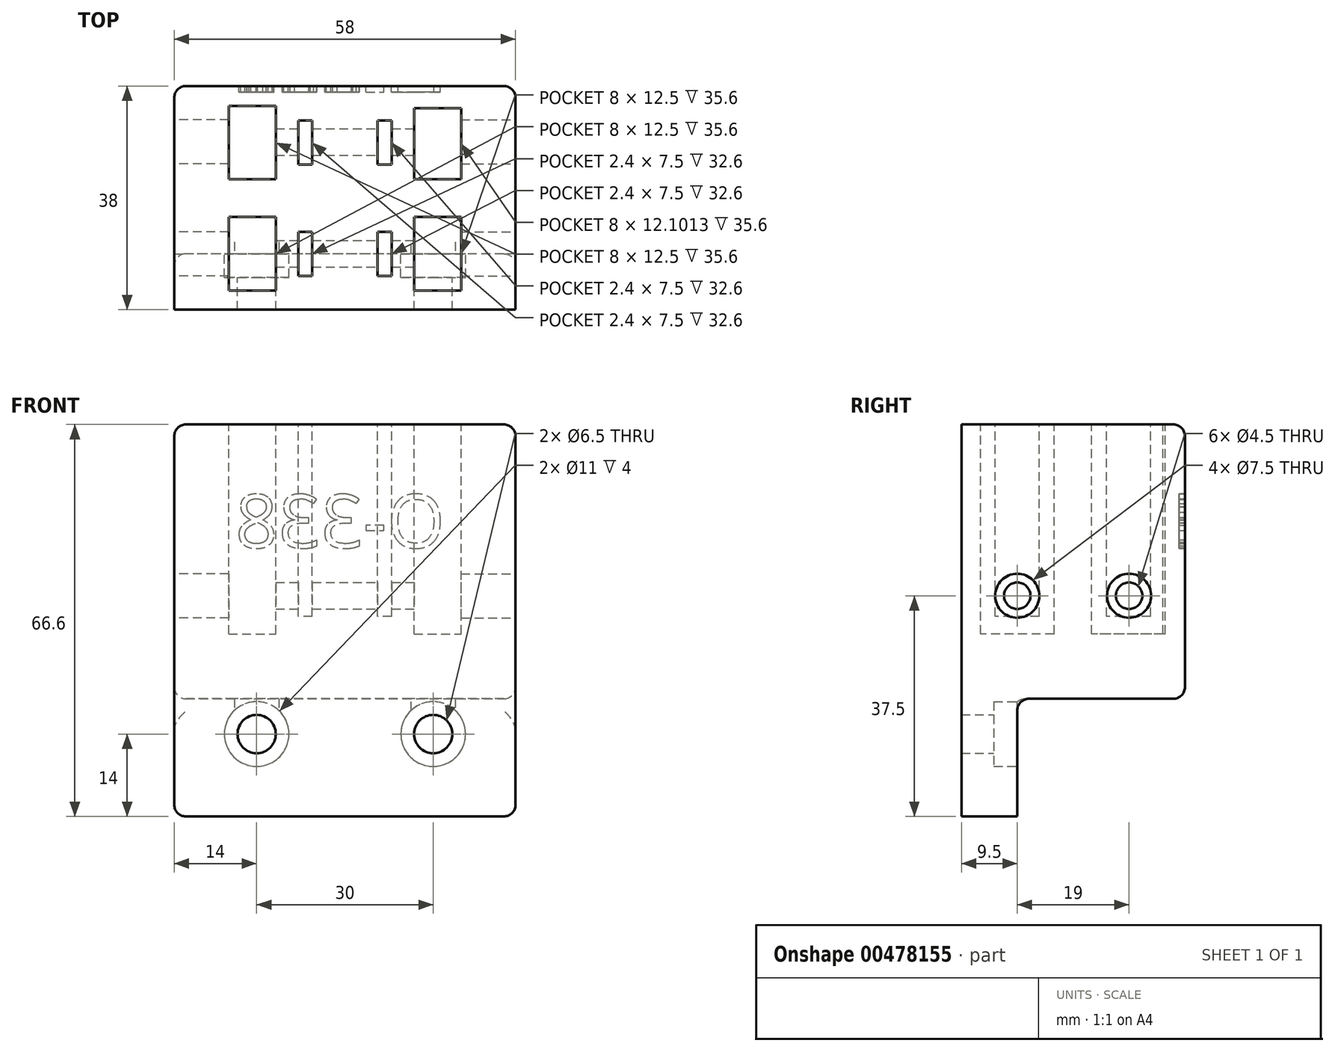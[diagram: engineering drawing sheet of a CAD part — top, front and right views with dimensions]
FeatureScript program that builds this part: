
annotation { "Feature Type Name" : "Feature", "Feature Type Description" : "" }
export const myFeature = defineFeature(function(context is Context, id is Id, definition is map)
    precondition{}
    {
        {
            var Q0;
            Q0=qCreatedBy(makeId("Top.planeOp"),FACE);
            var sketch = newSketch(context, id + "F0", { "sketchPlane" : qUnion([Q0])});
            skLineSegment(sketch, "E0.bottom", {"start": v(-29, 9.5) * mm, "end": v(29, 9.5) * mm});
            skLineSegment(sketch, "E0.top", {"start": v(-29, -9.5) * mm, "end": v(29, -9.5) * mm});
            skLineSegment(sketch, "E0.left", {"start": v(-29, 9.5) * mm, "end": v(-29, -9.5) * mm});
            skLineSegment(sketch, "E0.right", {"start": v(29, 9.5) * mm, "end": v(29, -9.5) * mm});
            skSolve(sketch);
        }
        {
            var Q0;
            Q0 = qSketchRegion(id + "F0", true);
            extrude(context, id + "F1", {"entities" : qUnion([Q0]), "depth" : 11 * mm});
        }
        {
            var Q0;
            Q0=makeQuery(id+"F1.opExtrude","CAP_FACE",FACE,{"disambiguationData":[OSD([sQuery(id+"F0.wireOp",EDGE,"E0.bottom"),sQuery(id+"F0.wireOp",EDGE,"E0.top"),sQuery(id+"F0.wireOp",EDGE,"E0.left"),sQuery(id+"F0.wireOp",EDGE,"E0.right"),sQuery(id+"F0.wireOp",EDGE,"AuSHMrTt-jpj0-5Ru2-xaIe-a4Oixfi13iDE"),sQuery(id+"F0.wireOp",EDGE,"9J5HWsQ0-lQpk-E1t6-wWkI-SOKKZm0BYfsw"),sQuery(id+"F0.wireOp",EDGE,"2GzKSPJo-uI2N-Esed-kJXd-WJqO7sIm6bVz"),sQuery(id+"F0.wireOp",EDGE,"DJKESrdY-mQTo-sUHj-6MfV-pHmhVGQO2tIG")])],"isStart":false});
            var sketch = newSketch(context, id + "F2", { "sketchPlane" : qUnion([Q0])});
            skLineSegment(sketch, "E1.bottom", {"start": v(-29, 9.5) * mm, "end": v(29, 9.5) * mm});
            skLineSegment(sketch, "E1.top", {"start": v(-29, -9.5) * mm, "end": v(29, -9.5) * mm});
            skLineSegment(sketch, "E1.left", {"start": v(-29, 9.5) * mm, "end": v(-29, -9.5) * mm});
            skLineSegment(sketch, "E1.right", {"start": v(29, 9.5) * mm, "end": v(29, -9.5) * mm});
            skPoint(sketch, "E1.middle", {"position": v(0, 0) * mm});
            skSolve(sketch);
        }
        {
            var Q0;
            Q0 = qSketchRegion(id + "F2", true);
            extrude(context, id + "F3", {"entities" : qUnion([Q0]), "operationType" : NewBodyOperationType.ADD, "depth" : 35.6 * mm});
        }
        {
            var Q0;
            Q0=makeQuery(id+"F3.opExtrude","CAP_FACE",FACE,{"disambiguationData":[OSD([sQuery(id+"F2.wireOp",EDGE,"E1.bottom"),sQuery(id+"F2.wireOp",EDGE,"E1.top"),sQuery(id+"F2.wireOp",EDGE,"E1.left"),sQuery(id+"F2.wireOp",EDGE,"E1.right")])],"isStart":false});
            var sketch = newSketch(context, id + "F4", { "sketchPlane" : qUnion([Q0])});
            skLineSegment(sketch, "E2.bottom", {"start": v(-19.75, 6.25) * mm, "end": v(-11.75, 6.25) * mm});
            skLineSegment(sketch, "E2.top", {"start": v(-19.75, -6.25) * mm, "end": v(-11.75, -6.25) * mm});
            skLineSegment(sketch, "E2.left", {"start": v(-19.75, 6.25) * mm, "end": v(-19.75, -6.25) * mm});
            skLineSegment(sketch, "E2.right", {"start": v(-11.75, 6.25) * mm, "end": v(-11.75, -6.25) * mm});
            skPoint(sketch, "E2.middle", {"position": v(-15.75, 0) * mm});
            skLineSegment(sketch, "E3.bottom", {"start": v(11.75, 6.25) * mm, "end": v(19.75, 6.25) * mm});
            skLineSegment(sketch, "E3.top", {"start": v(11.75, -6.25) * mm, "end": v(19.75, -6.25) * mm});
            skLineSegment(sketch, "E3.left", {"start": v(11.75, 6.25) * mm, "end": v(11.75, -6.25) * mm});
            skLineSegment(sketch, "E3.right", {"start": v(19.75, 6.25) * mm, "end": v(19.75, -6.25) * mm});
            skPoint(sketch, "E3.middle", {"position": v(15.75, 0) * mm});
            skSolve(sketch);
        }
        {
            var Q0;
            Q0 = qSketchRegion(id + "F4", true);
            extrude(context, id + "F5", {"entities" : qUnion([Q0]), "operationType" : NewBodyOperationType.REMOVE, "oppositeDirection" : true, "depth" : 35.6 * mm});
        }
        {
            var Q0;
            Q0=makeQuery(id+"F3.boolean.opBoolean","MERGE",FACE,{"derivedFrom":[makeQuery(id+"F1.opExtrude","SWEPT_FACE",FACE,{"disambiguationData":[OSD([sQuery(id+"F0.wireOp",EDGE,"E0.right")])]}),makeQuery(id+"F3.opExtrude","SWEPT_FACE",FACE,{"disambiguationData":[OSD([sQuery(id+"F2.wireOp",EDGE,"E1.right")])]})]});
            var sketch = newSketch(context, id + "F6", { "sketchPlane" : qUnion([Q0])});
            skCircle(sketch, "E4", {"center": v(0, 17.5) * mm, "radius": 2.25 * mm});
            skSolve(sketch);
        }
        {
            var Q0;
            Q0 = qSketchRegion(id + "F6", true);
            extrude(context, id + "F7", {"entities" : qUnion([Q0]), "operationType" : NewBodyOperationType.REMOVE, "endBound" : BoundingType.THROUGH_ALL, "oppositeDirection" : true, "depth" : 25 * mm});
        }
        {
            var Q0;
            Q0=makeQuery(id+"F3.opExtrude","CAP_FACE",FACE,{"disambiguationData":[OSD([sQuery(id+"F2.wireOp",EDGE,"E1.bottom"),sQuery(id+"F2.wireOp",EDGE,"E1.top"),sQuery(id+"F2.wireOp",EDGE,"E1.left"),sQuery(id+"F2.wireOp",EDGE,"E1.right")])],"isStart":false});
            var sketch = newSketch(context, id + "F8", { "sketchPlane" : qUnion([Q0])});
            skLineSegment(sketch, "E5.bottom", {"start": v(7.95, 3.75) * mm, "end": v(5.55, 3.75) * mm});
            skLineSegment(sketch, "E5.top", {"start": v(7.95, -3.75) * mm, "end": v(5.55, -3.75) * mm});
            skLineSegment(sketch, "E5.left", {"start": v(7.95, 3.75) * mm, "end": v(7.95, -3.75) * mm});
            skLineSegment(sketch, "E5.right", {"start": v(5.55, 3.75) * mm, "end": v(5.55, -3.75) * mm});
            skPoint(sketch, "E5.middle", {"position": v(6.75, 0) * mm});
            skLineSegment(sketch, "E6.bottom", {"start": v(-5.55, 3.75) * mm, "end": v(-7.95, 3.75) * mm});
            skLineSegment(sketch, "E6.top", {"start": v(-5.55, -3.75) * mm, "end": v(-7.95, -3.75) * mm});
            skLineSegment(sketch, "E6.left", {"start": v(-5.55, 3.75) * mm, "end": v(-5.55, -3.75) * mm});
            skLineSegment(sketch, "E6.right", {"start": v(-7.95, 3.75) * mm, "end": v(-7.95, -3.75) * mm});
            skPoint(sketch, "E6.middle", {"position": v(-6.75, 0) * mm});
            skSolve(sketch);
        }
        {
            var Q0;
            Q0 = qSketchRegion(id + "F8", true);
            extrude(context, id + "F9", {"entities" : qUnion([Q0]), "operationType" : NewBodyOperationType.REMOVE, "oppositeDirection" : true, "depth" : 32.6 * mm});
        }
        {
            var Q0;
            Q0=makeQuery(id+"F3.boolean.opBoolean","MERGE",FACE,{"derivedFrom":[makeQuery(id+"F1.opExtrude","SWEPT_FACE",FACE,{"disambiguationData":[OSD([sQuery(id+"F0.wireOp",EDGE,"E0.left")])]}),makeQuery(id+"F3.opExtrude","SWEPT_FACE",FACE,{"disambiguationData":[OSD([sQuery(id+"F2.wireOp",EDGE,"E1.left")])]})]});
            var sketch = newSketch(context, id + "F10", { "sketchPlane" : qUnion([Q0])});
            skCircle(sketch, "E7", {"center": v(0, 17.5) * mm, "radius": 3.75 * mm});
            skSolve(sketch);
        }
        {
            var Q0;
            Q0 = qSketchRegion(id + "F10", true);
            extrude(context, id + "F11", {"entities" : qUnion([Q0]), "operationType" : NewBodyOperationType.REMOVE, "oppositeDirection" : true, "depth" : 9.25 * mm});
        }
        {
            var Q0;
            Q0=makeQuery(id+"F3.boolean.opBoolean","MERGE",FACE,{"derivedFrom":[makeQuery(id+"F1.opExtrude","SWEPT_FACE",FACE,{"disambiguationData":[OSD([sQuery(id+"F0.wireOp",EDGE,"E0.right")])]}),makeQuery(id+"F3.opExtrude","SWEPT_FACE",FACE,{"disambiguationData":[OSD([sQuery(id+"F2.wireOp",EDGE,"E1.right")])]})]});
            var sketch = newSketch(context, id + "F12", { "sketchPlane" : qUnion([Q0])});
            skCircle(sketch, "E8", {"center": v(0, 17.5) * mm, "radius": 3.75 * mm});
            skSolve(sketch);
        }
        {
            var Q0;
            Q0 = qSketchRegion(id + "F12", true);
            extrude(context, id + "F13", {"entities" : qUnion([Q0]), "operationType" : NewBodyOperationType.REMOVE, "oppositeDirection" : true, "depth" : 9.25 * mm});
        }
        {
            var Q0;
            Q0 = qSketchRegion(id + "F0", true);
            extrude(context, id + "F14", {"entities" : qUnion([Q0]), "operationType" : NewBodyOperationType.ADD, "oppositeDirection" : true, "depth" : 20 * mm});
        }
        {
            var Q0;
            Q0=qCreatedBy(makeId("Top.planeOp"),FACE);
            var sketch = newSketch(context, id + "F15", { "sketchPlane" : qUnion([Q0])});
            skLineSegment(sketch, "E9.bottom", {"start": v(-29, 28.5) * mm, "end": v(29, 28.5) * mm});
            skLineSegment(sketch, "E9.top", {"start": v(-29, 9.5) * mm, "end": v(29, 9.5) * mm});
            skLineSegment(sketch, "E9.left", {"start": v(-29, 28.5) * mm, "end": v(-29, 9.5) * mm});
            skLineSegment(sketch, "E9.right", {"start": v(29, 28.5) * mm, "end": v(29, 9.5) * mm});
            skSolve(sketch);
        }
        {
            var Q0;
            Q0 = qSketchRegion(id + "F15", true);
            extrude(context, id + "F16", {"entities" : qUnion([Q0]), "operationType" : NewBodyOperationType.ADD, "depth" : 46.6 * mm});
        }
        {
            var Q0;
            Q0=makeQuery(id+"F16.boolean.opBoolean","MERGE",FACE,{"derivedFrom":[makeQuery(id+"F3.opExtrude","CAP_FACE",FACE,{"disambiguationData":[OSD([sQuery(id+"F2.wireOp",EDGE,"E1.bottom"),sQuery(id+"F2.wireOp",EDGE,"E1.top"),sQuery(id+"F2.wireOp",EDGE,"E1.left"),sQuery(id+"F2.wireOp",EDGE,"E1.right")])],"isStart":false}),makeQuery(id+"F16.opExtrude","CAP_FACE",FACE,{"disambiguationData":[OSD([sQuery(id+"F15.wireOp",EDGE,"E9.bottom"),sQuery(id+"F15.wireOp",EDGE,"E9.top"),sQuery(id+"F15.wireOp",EDGE,"E9.left"),sQuery(id+"F15.wireOp",EDGE,"E9.right")])],"isStart":false})]});
            var sketch = newSketch(context, id + "F17", { "sketchPlane" : qUnion([Q0])});
            skLineSegment(sketch, "E10.bottom", {"start": v(-19.75, 25.15) * mm, "end": v(-11.75, 25.15) * mm});
            skLineSegment(sketch, "E10.top", {"start": v(-19.75, 12.65) * mm, "end": v(-11.75, 12.65) * mm});
            skLineSegment(sketch, "E10.left", {"start": v(-19.75, 25.15) * mm, "end": v(-19.75, 12.65) * mm});
            skLineSegment(sketch, "E10.right", {"start": v(-11.75, 25.15) * mm, "end": v(-11.75, 12.65) * mm});
            skLineSegment(sketch, "E11.bottom", {"start": v(11.75, 24.75) * mm, "end": v(19.75, 24.75) * mm});
            skLineSegment(sketch, "E11.top", {"start": v(11.75, 12.65) * mm, "end": v(19.75, 12.65) * mm});
            skLineSegment(sketch, "E11.left", {"start": v(11.75, 24.75) * mm, "end": v(11.75, 12.65) * mm});
            skLineSegment(sketch, "E11.right", {"start": v(19.75, 24.75) * mm, "end": v(19.75, 12.65) * mm});
            skSolve(sketch);
        }
        {
            var Q0;
            Q0 = qSketchRegion(id + "F17", true);
            extrude(context, id + "F18", {"entities" : qUnion([Q0]), "operationType" : NewBodyOperationType.REMOVE, "oppositeDirection" : true, "depth" : 35.6 * mm});
        }
        {
            var Q0;
            {var subQ0=sQuery(id+"F0.wireOp",EDGE,"E0.right");var subQ2=sQuery(id+"F0.wireOp",EDGE,"E0.bottom");var subQ4=sQuery(id+"F2.wireOp",EDGE,"E1.right");Q0=makeQuery(id+"F16.boolean.opBoolean","MERGE",FACE,{"derivedFrom":[makeQuery(id+"F14.boolean.opBoolean","MERGE",FACE,{"derivedFrom":[makeQuery(id+"FXwZepqlZW6l2EH_1.boolean.opBoolean","SPLIT",FACE,{"disambiguationData":[TD([makeQuery(id+"F1.opExtrude","SWEPT_FACE",FACE,{"disambiguationData":[OSD([subQ2])]})])],"derivedFrom":makeQuery(id+"F3.boolean.opBoolean","MERGE",FACE,{"derivedFrom":[makeQuery(id+"F1.opExtrude","SWEPT_FACE",FACE,{"disambiguationData":[OSD([subQ0])]}),makeQuery(id+"F3.opExtrude","SWEPT_FACE",FACE,{"disambiguationData":[OSD([subQ4])]})]})}),makeQuery(id+"F14.opExtrude","SWEPT_FACE",FACE,{"disambiguationData":[OSD([subQ0])]})]}),makeQuery(id+"F16.opExtrude","SWEPT_FACE",FACE,{"disambiguationData":[OSD([sQuery(id+"F15.wireOp",EDGE,"E9.right")])]})]});}
            var sketch = newSketch(context, id + "F19", { "sketchPlane" : qUnion([Q0])});
            skCircle(sketch, "E12", {"center": v(19, 17.5) * mm, "radius": 2.25 * mm});
            skSolve(sketch);
        }
        {
            var Q0;
            Q0 = qSketchRegion(id + "F19", true);
            extrude(context, id + "F20", {"entities" : qUnion([Q0]), "operationType" : NewBodyOperationType.REMOVE, "endBound" : BoundingType.THROUGH_ALL, "oppositeDirection" : true, "depth" : 25 * mm});
        }
        {
            var Q0;
            Q0=makeQuery(id+"F16.boolean.opBoolean","MERGE",FACE,{"derivedFrom":[makeQuery(id+"F3.opExtrude","CAP_FACE",FACE,{"disambiguationData":[OSD([sQuery(id+"F2.wireOp",EDGE,"E1.bottom"),sQuery(id+"F2.wireOp",EDGE,"E1.top"),sQuery(id+"F2.wireOp",EDGE,"E1.left"),sQuery(id+"F2.wireOp",EDGE,"E1.right")])],"isStart":false}),makeQuery(id+"F16.opExtrude","CAP_FACE",FACE,{"disambiguationData":[OSD([sQuery(id+"F15.wireOp",EDGE,"E9.bottom"),sQuery(id+"F15.wireOp",EDGE,"E9.top"),sQuery(id+"F15.wireOp",EDGE,"E9.left"),sQuery(id+"F15.wireOp",EDGE,"E9.right")])],"isStart":false})]});
            var sketch = newSketch(context, id + "F21", { "sketchPlane" : qUnion([Q0])});
            skLineSegment(sketch, "E13.bottom", {"start": v(-7.95, 22.65) * mm, "end": v(-5.55, 22.65) * mm});
            skLineSegment(sketch, "E13.top", {"start": v(-7.95, 15.15) * mm, "end": v(-5.55, 15.15) * mm});
            skLineSegment(sketch, "E13.left", {"start": v(-7.95, 22.65) * mm, "end": v(-7.95, 15.15) * mm});
            skLineSegment(sketch, "E13.right", {"start": v(-5.55, 22.65) * mm, "end": v(-5.55, 15.15) * mm});
            skLineSegment(sketch, "E14.bottom", {"start": v(5.55, 22.65) * mm, "end": v(7.95, 22.65) * mm});
            skLineSegment(sketch, "E14.top", {"start": v(5.55, 15.15) * mm, "end": v(7.95, 15.15) * mm});
            skLineSegment(sketch, "E14.left", {"start": v(5.55, 22.65) * mm, "end": v(5.55, 15.15) * mm});
            skLineSegment(sketch, "E14.right", {"start": v(7.95, 22.65) * mm, "end": v(7.95, 15.15) * mm});
            skSolve(sketch);
        }
        {
            var Q0;
            Q0 = qSketchRegion(id + "F21", true);
            extrude(context, id + "F22", {"entities" : qUnion([Q0]), "operationType" : NewBodyOperationType.REMOVE, "oppositeDirection" : true, "depth" : 32.6 * mm});
        }
        {
            var Q0;
            {var subQ0=sQuery(id+"F0.wireOp",EDGE,"E0.right");var subQ2=sQuery(id+"F0.wireOp",EDGE,"E0.bottom");var subQ4=sQuery(id+"F2.wireOp",EDGE,"E1.right");Q0=makeQuery(id+"F16.boolean.opBoolean","MERGE",FACE,{"derivedFrom":[makeQuery(id+"F14.boolean.opBoolean","MERGE",FACE,{"derivedFrom":[makeQuery(id+"FXwZepqlZW6l2EH_1.boolean.opBoolean","SPLIT",FACE,{"disambiguationData":[TD([makeQuery(id+"F1.opExtrude","SWEPT_FACE",FACE,{"disambiguationData":[OSD([subQ2])]})])],"derivedFrom":makeQuery(id+"F3.boolean.opBoolean","MERGE",FACE,{"derivedFrom":[makeQuery(id+"F1.opExtrude","SWEPT_FACE",FACE,{"disambiguationData":[OSD([subQ0])]}),makeQuery(id+"F3.opExtrude","SWEPT_FACE",FACE,{"disambiguationData":[OSD([subQ4])]})]})}),makeQuery(id+"F14.opExtrude","SWEPT_FACE",FACE,{"disambiguationData":[OSD([subQ0])]})]}),makeQuery(id+"F16.opExtrude","SWEPT_FACE",FACE,{"disambiguationData":[OSD([sQuery(id+"F15.wireOp",EDGE,"E9.right")])]})]});}
            var sketch = newSketch(context, id + "F23", { "sketchPlane" : qUnion([Q0])});
            skCircle(sketch, "E15", {"center": v(19, 17.5) * mm, "radius": 3.75 * mm});
            skSolve(sketch);
        }
        {
            var Q0;
            Q0 = qSketchRegion(id + "F23", true);
            extrude(context, id + "F24", {"entities" : qUnion([Q0]), "operationType" : NewBodyOperationType.REMOVE, "oppositeDirection" : true, "depth" : 10 * mm});
        }
        {
            var Q0;
            {var subQ0=sQuery(id+"F0.wireOp",EDGE,"E0.left");Q0=makeQuery(id+"F16.boolean.opBoolean","MERGE",FACE,{"derivedFrom":[makeQuery(id+"F14.boolean.opBoolean","MERGE",FACE,{"derivedFrom":[makeQuery(id+"F3.boolean.opBoolean","MERGE",FACE,{"derivedFrom":[makeQuery(id+"F1.opExtrude","SWEPT_FACE",FACE,{"disambiguationData":[OSD([subQ0])]}),makeQuery(id+"F3.opExtrude","SWEPT_FACE",FACE,{"disambiguationData":[OSD([sQuery(id+"F2.wireOp",EDGE,"E1.left")])]})]}),makeQuery(id+"F14.opExtrude","SWEPT_FACE",FACE,{"disambiguationData":[OSD([subQ0])]})]}),makeQuery(id+"F16.opExtrude","SWEPT_FACE",FACE,{"disambiguationData":[OSD([sQuery(id+"F15.wireOp",EDGE,"E9.left")])]})]});}
            var sketch = newSketch(context, id + "F25", { "sketchPlane" : qUnion([Q0])});
            skCircle(sketch, "E16", {"center": v(-19, 17.5) * mm, "radius": 3.75 * mm});
            skSolve(sketch);
        }
        {
            var Q0;
            Q0 = qSketchRegion(id + "F25", true);
            extrude(context, id + "F26", {"entities" : qUnion([Q0]), "operationType" : NewBodyOperationType.REMOVE, "oppositeDirection" : true, "depth" : 10 * mm});
        }
        {
            var Q0;
            Q0=makeQuery(id+"F16.opExtrude","SWEPT_FACE",FACE,{"disambiguationData":[OSD([sQuery(id+"F15.wireOp",EDGE,"E9.bottom")])]});
            var sketch = newSketch(context, id + "F27", { "sketchPlane" : qUnion([Q0])});
            skText(sketch, "E17", { "text": "O-338", "fontName": "OpenSans-Regular.ttf"});
            const initialGuessF27  = {"E17": [-0.017, 0.02564, 1, 0, 0.00912]};
            skSetInitialGuess(sketch, initialGuessF27);
            skSolve(sketch);
        }
        {
            var Q0;
            Q0 = qSketchRegion(id + "F27", true);
            extrude(context, id + "F28", {"entities" : qUnion([Q0]), "operationType" : NewBodyOperationType.REMOVE, "oppositeDirection" : true, "depth" : 1 * mm});
        }
        {
            var Q0;
            {var subQ0=sQuery(id+"F0.wireOp",EDGE,"E0.bottom");Q0=makeQuery(id+"F14.boolean.opBoolean","MERGE",FACE,{"derivedFrom":[makeQuery(id+"F3.boolean.opBoolean","MERGE",FACE,{"derivedFrom":[makeQuery(id+"F1.opExtrude","SWEPT_FACE",FACE,{"disambiguationData":[OSD([subQ0])]}),makeQuery(id+"F3.opExtrude","SWEPT_FACE",FACE,{"disambiguationData":[OSD([sQuery(id+"F2.wireOp",EDGE,"E1.bottom")])]})]}),makeQuery(id+"F14.opExtrude","SWEPT_FACE",FACE,{"disambiguationData":[OSD([subQ0])]})]});}
            var sketch = newSketch(context, id + "F29", { "sketchPlane" : qUnion([Q0])});
            skCircle(sketch, "E18", {"center": v(-15, -6) * mm, "radius": 3.25 * mm});
            skCircle(sketch, "E19", {"center": v(15, -6) * mm, "radius": 3.25 * mm});
            skSolve(sketch);
        }
        {
            var Q0;
            Q0 = qSketchRegion(id + "F29", true);
            extrude(context, id + "F30", {"entities" : qUnion([Q0]), "operationType" : NewBodyOperationType.REMOVE, "endBound" : BoundingType.THROUGH_ALL, "oppositeDirection" : true, "depth" : 25 * mm});
        }
        {
            var Q0;
            {var subQ0=sQuery(id+"F0.wireOp",EDGE,"E0.bottom");Q0=makeQuery(id+"F14.boolean.opBoolean","MERGE",FACE,{"derivedFrom":[makeQuery(id+"F3.boolean.opBoolean","MERGE",FACE,{"derivedFrom":[makeQuery(id+"F1.opExtrude","SWEPT_FACE",FACE,{"disambiguationData":[OSD([subQ0])]}),makeQuery(id+"F3.opExtrude","SWEPT_FACE",FACE,{"disambiguationData":[OSD([sQuery(id+"F2.wireOp",EDGE,"E1.bottom")])]})]}),makeQuery(id+"F14.opExtrude","SWEPT_FACE",FACE,{"disambiguationData":[OSD([subQ0])]})]});}
            var sketch = newSketch(context, id + "F31", { "sketchPlane" : qUnion([Q0])});
            skCircle(sketch, "E20", {"center": v(-15, -6) * mm, "radius": 5.5 * mm});
            skCircle(sketch, "E21", {"center": v(15, -6) * mm, "radius": 5.5 * mm});
            skSolve(sketch);
        }
        {
            var Q0;
            Q0 = qSketchRegion(id + "F31", true);
            extrude(context, id + "F32", {"entities" : qUnion([Q0]), "operationType" : NewBodyOperationType.REMOVE, "oppositeDirection" : true, "depth" : 13.5 * mm});
        }
        {
            var Q0;
            Q0=qCreatedBy(makeId("Front.planeOp"),FACE);
            var sketch = newSketch(context, id + "F33", { "sketchPlane" : qUnion([Q0])});
            skLineSegment(sketch, "E22.bottom", {"start": v(29, 0) * mm, "end": v(-29, 0) * mm});
            skLineSegment(sketch, "E22.top", {"start": v(29, -20) * mm, "end": v(-29, -20) * mm});
            skLineSegment(sketch, "E22.left", {"start": v(29, 0) * mm, "end": v(29, -20) * mm});
            skLineSegment(sketch, "E22.right", {"start": v(-29, 0) * mm, "end": v(-29, -20) * mm});
            skSolve(sketch);
        }
        {
            var Q0;
            Q0 = qSketchRegion(id + "F33", true);
            extrude(context, id + "F34", {"entities" : qUnion([Q0]), "operationType" : NewBodyOperationType.REMOVE, "endBound" : BoundingType.THROUGH_ALL, "oppositeDirection" : true, "depth" : 25 * mm});
        }
        {
            var Q0;
            Q0=makeQuery(id+"F16.boolean.opBoolean","MERGE",EDGE,{"derivedFrom":[makeQuery(id+"F3.opExtrude","CAP_EDGE",EDGE,{"disambiguationData":[OSD([sQuery(id+"F2.wireOp",EDGE,"E1.right")])],"isStart":false}),makeQuery(id+"F16.opExtrude","CAP_EDGE",EDGE,{"disambiguationData":[OSD([sQuery(id+"F15.wireOp",EDGE,"E9.right")])],"isStart":false})]});
            var Q1;
            Q1=makeQuery(id+"F16.boolean.opBoolean","MERGE",EDGE,{"derivedFrom":[makeQuery(id+"F3.opExtrude","CAP_EDGE",EDGE,{"disambiguationData":[OSD([sQuery(id+"F2.wireOp",EDGE,"E1.left")])],"isStart":false}),makeQuery(id+"F16.opExtrude","CAP_EDGE",EDGE,{"disambiguationData":[OSD([sQuery(id+"F15.wireOp",EDGE,"E9.left")])],"isStart":false})]});
            var Q2;
            Q2=makeQuery(id+"F16.opExtrude","SWEPT_EDGE",EDGE,{"disambiguationData":[OSD([sQuery(id+"F15.wireOp",EDGE,"E9.bottom"),sQuery(id+"F15.wireOp",EDGE,"E9.left")])]});
            var Q3;
            Q3=makeQuery(id+"F16.opExtrude","CAP_EDGE",EDGE,{"disambiguationData":[OSD([sQuery(id+"F15.wireOp",EDGE,"E9.bottom")])],"isStart":false});
            var Q4;
            Q4=makeQuery(id+"F16.opExtrude","CAP_EDGE",EDGE,{"disambiguationData":[OSD([sQuery(id+"F15.wireOp",EDGE,"E9.bottom")])],"isStart":true});
            var Q5;
            Q5=makeQuery(id+"F34.boolean.opBoolean","MERGE",EDGE,{"derivedFrom":[makeQuery(id+"F16.opExtrude","CAP_EDGE",EDGE,{"disambiguationData":[OSD([sQuery(id+"F15.wireOp",EDGE,"E9.left")])],"isStart":true}),makeQuery(id+"F34.opExtrude","SWEPT_EDGE",EDGE,{"disambiguationData":[OSD([sQuery(id+"F33.wireOp",EDGE,"E22.bottom"),sQuery(id+"F33.wireOp",EDGE,"E22.right")])]})]});
            var Q6;
            Q6=makeQuery(id+"F34.boolean.opBoolean","COPY",EDGE,{"derivedFrom":makeQuery(id+"F34.opExtrude","CAP_EDGE",EDGE,{"disambiguationData":[OSD([sQuery(id+"F33.wireOp",EDGE,"E22.right")])],"isStart":true})});
            var Q7;
            Q7=makeQuery(id+"F34.boolean.opBoolean","COPY",EDGE,{"derivedFrom":makeQuery(id+"F34.opExtrude","CAP_EDGE",EDGE,{"disambiguationData":[OSD([sQuery(id+"F33.wireOp",EDGE,"E22.top")])],"isStart":true})});
            var Q8;
            Q8=makeQuery(id+"F14.opExtrude","CAP_EDGE",EDGE,{"disambiguationData":[OSD([sQuery(id+"F0.wireOp",EDGE,"E0.left")])],"isStart":false});
            var Q9;
            Q9=makeQuery(id+"F14.opExtrude","CAP_EDGE",EDGE,{"disambiguationData":[OSD([sQuery(id+"F0.wireOp",EDGE,"E0.right")])],"isStart":false});
            var Q10;
            Q10=makeQuery(id+"F34.boolean.opBoolean","MERGE",FACE,{"derivedFrom":[makeQuery(id+"F16.opExtrude","CAP_FACE",FACE,{"disambiguationData":[OSD([sQuery(id+"F15.wireOp",EDGE,"E9.bottom"),sQuery(id+"F15.wireOp",EDGE,"E9.top"),sQuery(id+"F15.wireOp",EDGE,"E9.left"),sQuery(id+"F15.wireOp",EDGE,"E9.right")])],"isStart":true}),makeQuery(id+"F34.opExtrude","SWEPT_FACE",FACE,{"disambiguationData":[OSD([sQuery(id+"F33.wireOp",EDGE,"E22.bottom")])]})]});
            var Q11;
            Q11=makeQuery(id+"F16.opExtrude","SWEPT_EDGE",EDGE,{"disambiguationData":[OSD([sQuery(id+"F15.wireOp",EDGE,"E9.bottom"),sQuery(id+"F15.wireOp",EDGE,"E9.right")])]});
            fillet(context, id + "F35", {"entities" : qUnion([Q0, Q1, Q2, Q3, Q4, Q5, Q6, Q7, Q8, Q9, Q10, Q11]), "radius" : 2 * mm, "tangentPropagation" : true, "allowEdgeOverflow" : false});
        }
    });
